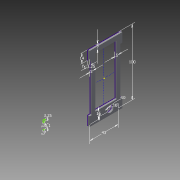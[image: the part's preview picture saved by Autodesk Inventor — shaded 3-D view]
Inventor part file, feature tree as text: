
AUTODESK INVENTOR PART (.ipt)
format: ipt  version: 2013 (Build 170138000, 138)  size: 113,664 bytes
history: native  units: mm
features: extrude x3, sketch x1
ambient origin geometry x8: Origin, YZ Plane, XZ Plane, XY Plane, X Axis, Y Axis, Z Axis, Center Point
bodies: Solid1 (feature_tree)
feature tree (4):
  sketch  "Sketch1"  dims[d0=3.0mm d2=3.0mm d4=43.0mm d5=100.0mm d9=7.0mm d10=16.0mm d11=5.0mm d12=5.0mm d13=10.0mm d15=3.0mm d16=3.25mm d17=14.0mm d18=3.25mm d19=0.0mm d20=3.25mm d21=0.0mm d22=3.25mm d23=0.0mm d24=10.0mm]
  extrude  "Extrusion1"  Depth=3.0mm
  extrude  "Extrusion2"  Depth=43.0mm
  extrude  "Extrusion3"  Depth=100.0mm
